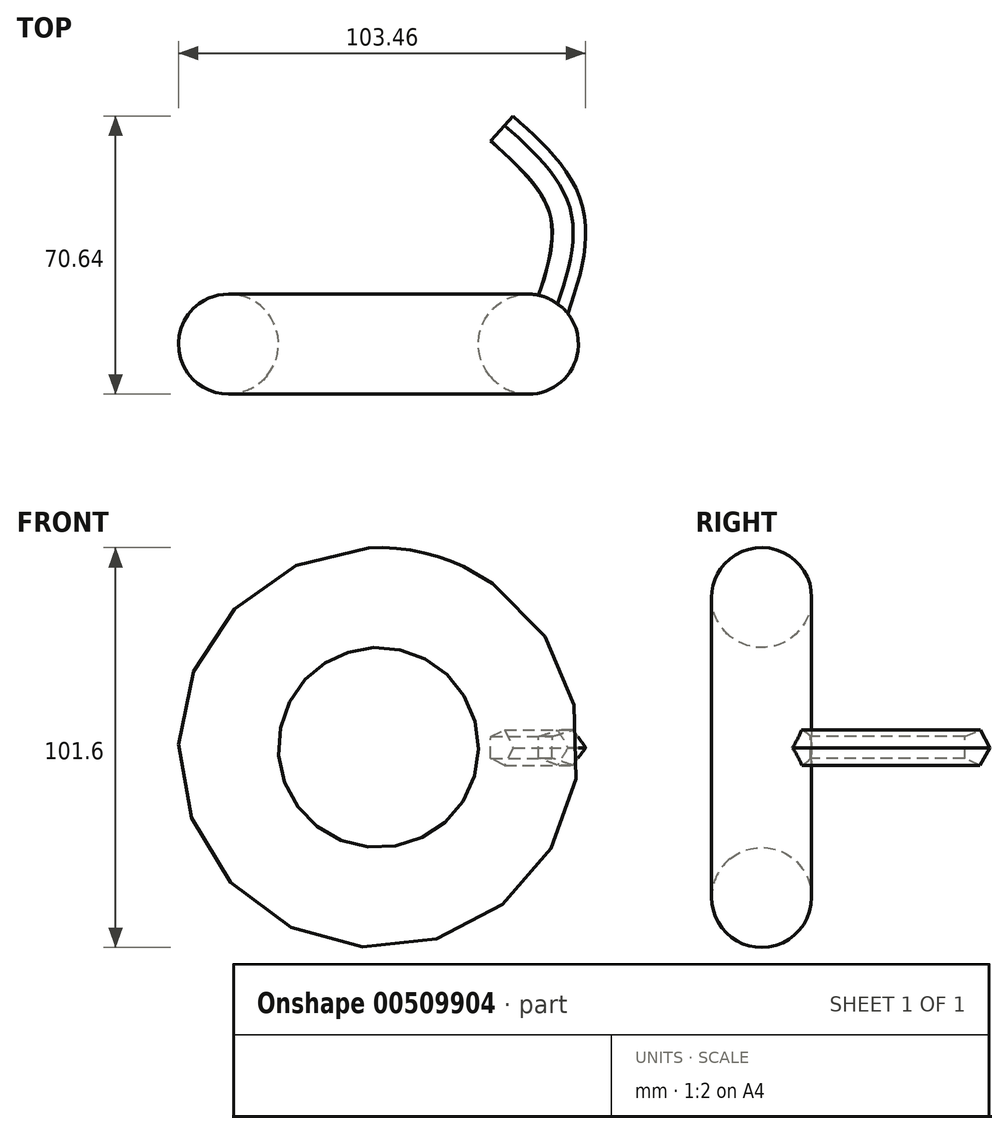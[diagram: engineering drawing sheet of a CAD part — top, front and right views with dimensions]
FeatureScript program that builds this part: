
annotation { "Feature Type Name" : "Feature", "Feature Type Description" : "" }
export const myFeature = defineFeature(function(context is Context, id is Id, definition is map)
    precondition{}
    {
        {
            var Q0;
            Q0=qCreatedBy(makeId("Top.planeOp"),FACE);
            var sketch = newSketch(context, id + "F0", { "sketchPlane" : qUnion([Q0])});
            skCircle(sketch, "E0", {"center": v(-33, -11.42) * mm, "radius": 12.7 * mm});
            skLineSegment(sketch, "E1", {"start": v(-33, -11.42) * mm, "end": v(5.1, -11.42) * mm, "construction": true});
            skLineSegment(sketch, "E2", {"start": v(5.1, 10.72) * mm, "end": v(5.1, -31.77) * mm, "construction": true});
            skPoint(sketch, "E3", {"position": v(-45.7, -11.42) * mm});
            skPoint(sketch, "E4", {"position": v(-33, -24.12) * mm});
            skPoint(sketch, "E5", {"position": v(5.1, -31.77) * mm});
            skFitSpline(sketch, "E6", {"points": [v(36.17, 43.03) * mm, v(52.45, 22.1) * mm, v(47.33, -6.05) * mm], "startDerivative": vector(43.8, -39.6) * mm, "endDerivative": vector(-21.06, -58.44) * mm});
            skSolve(sketch);
        }
        {
            var Q0;
            Q0=makeQuery(id+"F0.imprint","IMPRINT",FACE,{"disambiguationData":[TD([[makeQuery(id+"F0.imprint","IMPRINT",EDGE,{"derivedFrom":sQuery(id+"F0.wireOp",EDGE,"E0")}),1.0]])]});
            var Q1;
            Q1=sQuery(id+"F0.wireOp",EDGE,"E2");
            revolve(context, id + "F1", {"entities" : qUnion([Q0]), "axis" : qUnion([Q1]), "revolveType" : RevolveType.FULL});
        }
        {
            var Q0;
            Q0=sQuery(id+"F0.wireOp",EDGE,"E2");
            cPlane(context, id + "F2", {"entities" : qUnion([Q0]), "cplaneType" : CPlaneType.LINE_ANGLE, "offset" : 25.4 * mm, "angle" : 135 * degree, "width" : 152.4 * mm, "height" : 152.4 * mm});
        }
        {
            var Q0;
            Q0=qCreatedBy(id+"F2.planeOp",FACE);
            var sketch = newSketch(context, id + "F3", { "sketchPlane" : qUnion([Q0])});
            skPoint(sketch, "E7", {"position": v(-35.4, 21.49) * mm});
            skSolve(sketch);
        }
        {
            var Q0;
            Q0=sQuery(id+"F0.wireOp",VERTEX,"E5");
            var Q1;
            Q1=sQuery(id+"F0.wireOp",EDGE,"E2");
            cPlane(context, id + "F4", {"entities" : qUnion([Q0, Q1]), "cplaneType" : CPlaneType.LINE_POINT, "offset" : 25.4 * mm, "width" : 152.4 * mm, "height" : 152.4 * mm});
        }
        {
            var Q0;
            Q0=sQuery(id+"F0.wireOp",EDGE,"E6");
            var Q1;
            Q1=sQuery(id+"F0.wireOp",VERTEX,"E6.0.internal");
            cPlane(context, id + "F5", {"entities" : qUnion([Q0, Q1]), "cplaneType" : CPlaneType.CURVE_POINT, "offset" : 25.4 * mm, "width" : 152.4 * mm, "height" : 152.4 * mm});
        }
        {
            var Q0;
            Q0=qCreatedBy(id+"F5.planeOp",FACE);
            var sketch = newSketch(context, id + "F6", { "sketchPlane" : qUnion([Q0])});
            skCircle(sketch, "E8.cCircle", {"center": v(56.17, 0) * mm, "radius": 3.81 * mm, "construction": true});
            skLineSegment(sketch, "E8.0", {"start": v(52.4, 2.81) * mm, "end": v(57.68, 4.46) * mm});
            skLineSegment(sketch, "E8.1", {"start": v(57.68, 4.46) * mm, "end": v(60.88, -0.05) * mm});
            skLineSegment(sketch, "E8.2", {"start": v(60.88, -0.05) * mm, "end": v(57.58, -4.5) * mm});
            skLineSegment(sketch, "E8.3", {"start": v(57.58, -4.5) * mm, "end": v(52.33, -2.72) * mm});
            skLineSegment(sketch, "E8.4", {"start": v(52.33, -2.72) * mm, "end": v(52.4, 2.81) * mm});
            skPoint(sketch, "E8.0.midPoint", {"position": v(55.04, 3.64) * mm});
            skSolve(sketch);
        }
        {
            var Q0;
            Q0=makeQuery(id+"F6.imprint","IMPRINT",FACE,{"disambiguationData":[TD([[makeQuery(id+"F6.imprint","IMPRINT",EDGE,{"derivedFrom":sQuery(id+"F6.wireOp",EDGE,"E8.0")}),-1.0]])]});
            var Q1;
            Q1=sQuery(id+"F0.wireOp",EDGE,"E6");
            sweep(context, id + "F7", {"operationType" : NewBodyOperationType.ADD, "profiles" : qUnion([Q0]), "path" : qUnion([Q1])});
        }
    });
